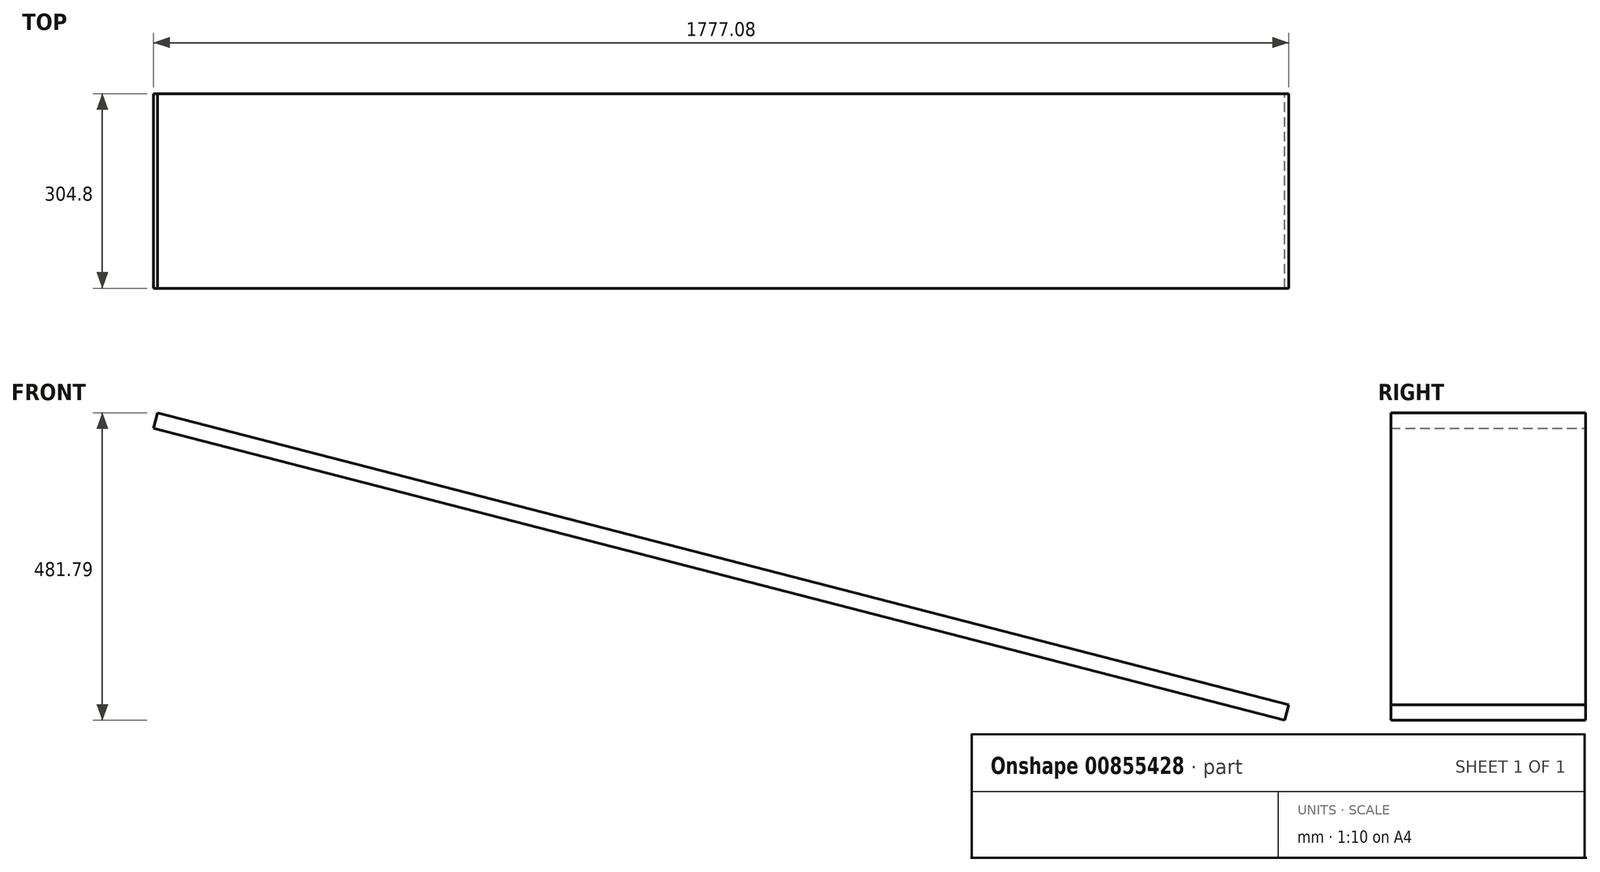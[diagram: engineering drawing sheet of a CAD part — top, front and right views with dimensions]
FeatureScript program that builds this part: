
annotation { "Feature Type Name" : "Feature", "Feature Type Description" : "" }
export const myFeature = defineFeature(function(context is Context, id is Id, definition is map)
    precondition{}
    {
        {
            var Q0;
            Q0=qCreatedBy(makeId("Front.planeOp"),FACE);
            var sketch = newSketch(context, id + "F0", { "sketchPlane" : qUnion([Q0])});
            skLineSegment(sketch, "E0", {"start": v(0, 0) * mm, "end": v(0, -457.2) * mm, "construction": true});
            skLineSegment(sketch, "E1", {"start": v(0, 0) * mm, "end": v(1770.73, -457.2) * mm});
            skLineSegment(sketch, "E2.0", {"start": v(6.35, 24.6) * mm, "end": v(1777.08, -432.6) * mm});
            skLineSegment(sketch, "E3", {"start": v(1770.73, -457.2) * mm, "end": v(1777.08, -432.6) * mm});
            skLineSegment(sketch, "E4", {"start": v(6.35, 24.6) * mm, "end": v(0, 0) * mm});
            skSolve(sketch);
        }
        {
            var Q0;
            Q0=qSketchRegion(id+"F0",true);
            extrude(context, id + "F1", {"entities" : qUnion([Q0]), "endBound" : BoundingType.SYMMETRIC, "depth" : 304.8 * mm, "offsetDistance" : 25.4 * mm});
        }
    });
